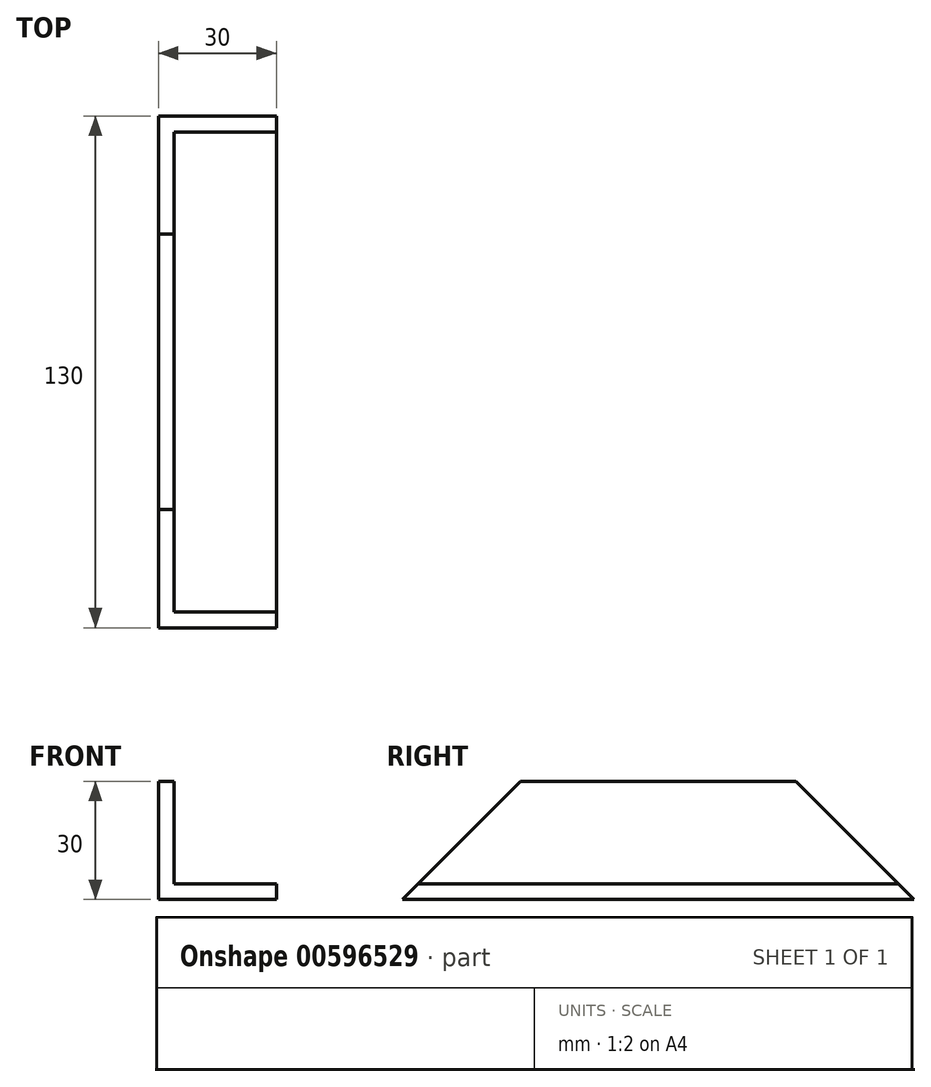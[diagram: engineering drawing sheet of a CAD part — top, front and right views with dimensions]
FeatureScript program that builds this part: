
annotation { "Feature Type Name" : "Feature", "Feature Type Description" : "" }
export const myFeature = defineFeature(function(context is Context, id is Id, definition is map)
    precondition{}
    {
        {
            var Q0;
            Q0=qCreatedBy(makeId("Front.planeOp"),FACE);
            var sketch = newSketch(context, id + "F0", { "sketchPlane" : qUnion([Q0])});
            skLineSegment(sketch, "E0", {"start": v(0, 0) * mm, "end": v(0, 30) * mm});
            skLineSegment(sketch, "E1", {"start": v(0, 30) * mm, "end": v(4, 30) * mm});
            skLineSegment(sketch, "E2", {"start": v(4, 30) * mm, "end": v(4, 4) * mm});
            skLineSegment(sketch, "E3", {"start": v(4, 4) * mm, "end": v(30, 4) * mm});
            skLineSegment(sketch, "E4", {"start": v(30, 4) * mm, "end": v(30, 0) * mm});
            skLineSegment(sketch, "E5", {"start": v(30, 0) * mm, "end": v(0, 0) * mm});
            skSolve(sketch);
        }
        {
            var Q0;
            Q0=makeQuery(id+"F0.imprint","IMPRINT",FACE,{"disambiguationData":[TD([[makeQuery(id+"F0.imprint","IMPRINT",EDGE,{"derivedFrom":sQuery(id+"F0.wireOp",EDGE,"E0")}),-1.0]])]});
            extrude(context, id + "F1", {"entities" : qUnion([Q0]), "depth" : 130 * mm, "offsetDistance" : 25 * mm});
        }
        {
            var Q0;
            Q0=makeQuery(id+"F1.opExtrude","SWEPT_FACE",FACE,{"disambiguationData":[OSD([sQuery(id+"F0.wireOp",EDGE,"E0")])]});
            var sketch = newSketch(context, id + "F2", { "sketchPlane" : qUnion([Q0])});
            skLineSegment(sketch, "E6", {"start": v(0, 0) * mm, "end": v(30, 30) * mm});
            skLineSegment(sketch, "E7", {"start": v(130, 0) * mm, "end": v(100, 30) * mm});
            skSolve(sketch);
        }
        {
            var Q0;
            {var subQ0=sQuery(id+"F2.wireOp",EDGE,"E6");Q0=makeQuery(id+"F2.imprint","IMPRINT",FACE,{"disambiguationData":[TD([[makeQuery(id+"F2.imprint","IMPRINT",EDGE,{"derivedFrom":subQ0}),1.0]])]});}
            var Q1;
            {var subQ0=sQuery(id+"F2.wireOp",EDGE,"E7");Q1=makeQuery(id+"F2.imprint","IMPRINT",FACE,{"disambiguationData":[TD([[makeQuery(id+"F2.imprint","IMPRINT",EDGE,{"derivedFrom":subQ0}),-1.0]])]});}
            extrude(context, id + "F3", {"entities" : qUnion([Q0, Q1]), "operationType" : NewBodyOperationType.REMOVE, "oppositeDirection" : true, "depth" : 50 * mm, "offsetDistance" : 25 * mm});
        }
    });
